# Revit family: Haworth_CabanaLounge_ChaiseLounge_AP_PRELIMINARY
name_source: partatom
category: Furniture
revit_build: Autodesk Revit 2018 (Build: 20170223_1515(x64)
units: mm (PartAtom-declared; Revit-internal decimal feet)

## family parameters
Always vertical = Yes
Cut with Voids When Loaded = No
OmniClass Number = 23.40.70.14.64.21
OmniClass Title = Systems Furniture
Room Calculation Point = No
Shared = No
Work Plane-Based = No

## types (3) — shared parameters
Assembly Code = E2020200
Back Width = 762 mm  [stored 2.5 ft]
Description = Haworth - Cabana Lounge - Chaise Lounge
Leg Offset = 70 mm  [stored 0.229659 ft]
Manufacturer = Haworth
Model = SECBHN
Revision Number = 1
Screen Width = 813 mm
Seat Depth = 762 mm  [stored 2.5 ft]
Seat Height = 459 mm  [stored 1.50591 ft]
Seat Width = 1524 mm  [stored 5 ft]
Size = Verify Final Dim. w/ Haworth
URL = https://www.haworth.com
URL - Product = https://www.haworth.com
Warranty = http://www.haworth.com

## per-type parameters (varying)
| type | Actual Depth | Actual Height | Actual Width | No Screen | With Screen |
| High Screen | 813 mm | 1372 mm  [stored 4.50131 ft] | 1575 mm  [stored 5.16732 ft] | No | Yes |
| Low Screen | 813 mm | 1067 mm  [stored 3.50066 ft] | 1575 mm  [stored 5.16732 ft] | No | Yes |
| No Screen | 762 mm  [stored 2.5 ft] | 772 mm  [stored 2.53281 ft] | 1524 mm  [stored 5 ft] | Yes | No |

type visibility flags (boolean, named after types; folded from table):
- High Screen: Yes: High Screen
- Low Screen: Yes: Low Screen
- No Screen: Yes: (none)

note: [stored X ft] marks values corroborated as IEEE doubles in the binary element streams (Revit-internal decimal feet)

## geometry (parser evidence)
native form markers: Extrusion x1, Sweep x13
no freeform markers — native parametric forms only
